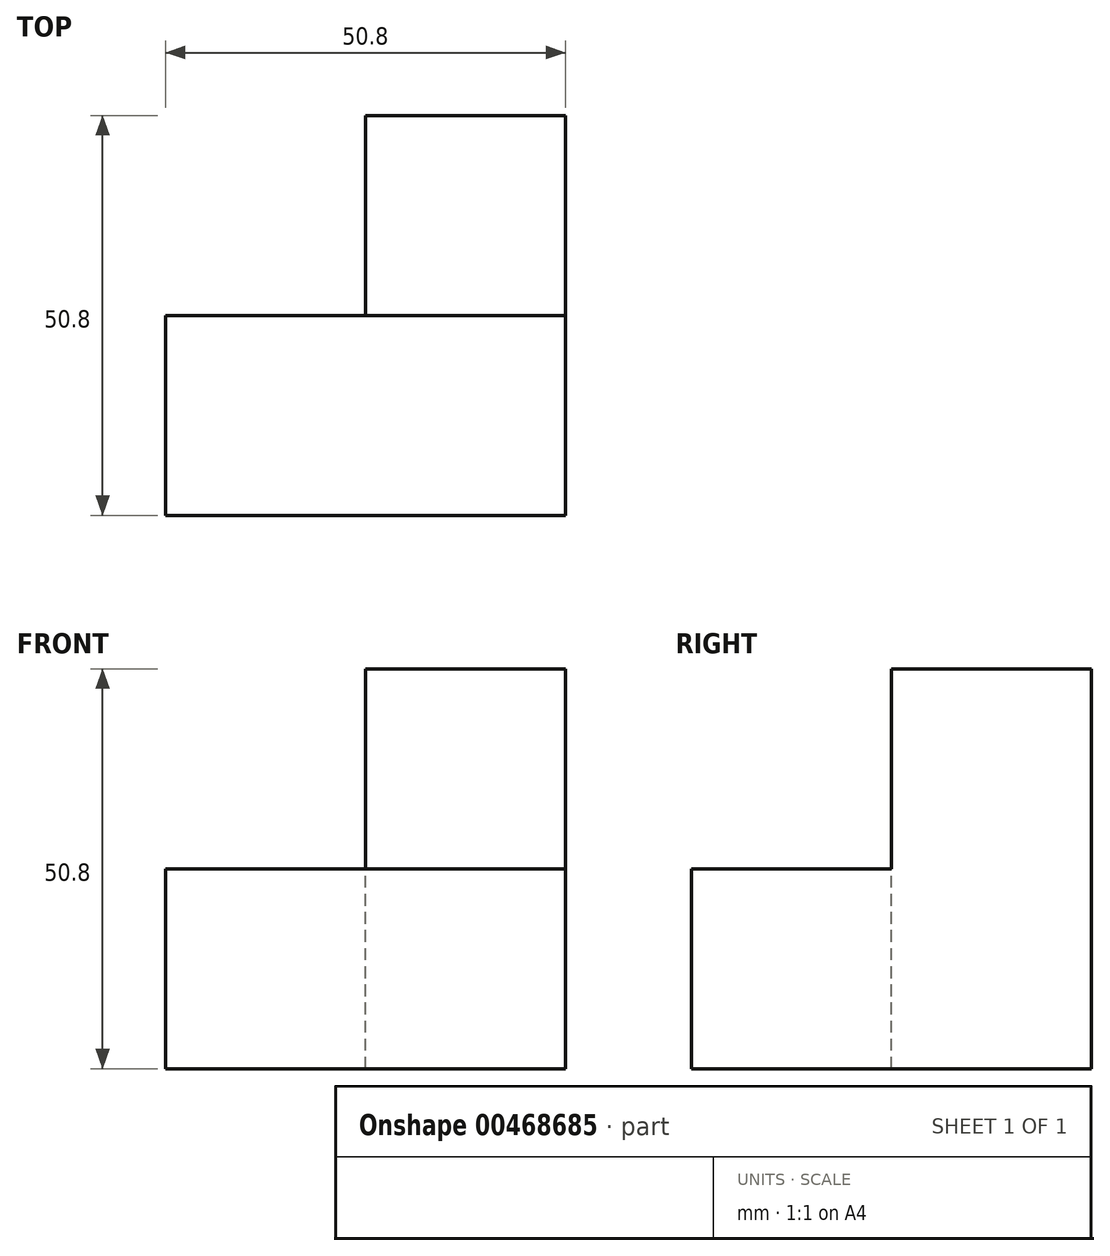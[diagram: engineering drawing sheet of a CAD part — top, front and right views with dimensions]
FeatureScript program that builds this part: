
annotation { "Feature Type Name" : "Feature", "Feature Type Description" : "" }
export const myFeature = defineFeature(function(context is Context, id is Id, definition is map)
    precondition{}
    {
        {
            var Q0;
            Q0=qCreatedBy(makeId("Front.planeOp"),FACE);
            var sketch = newSketch(context, id + "F0", { "sketchPlane" : qUnion([Q0])});
            skLineSegment(sketch, "E0.bottom", {"start": v(-25.4, 0) * mm, "end": v(25.4, 0) * mm});
            skLineSegment(sketch, "E0.top", {"start": v(-25.4, 25.4) * mm, "end": v(25.4, 25.4) * mm});
            skLineSegment(sketch, "E0.left", {"start": v(-25.4, 0) * mm, "end": v(-25.4, 25.4) * mm});
            skLineSegment(sketch, "E0.right", {"start": v(25.4, 0) * mm, "end": v(25.4, 25.4) * mm});
            skSolve(sketch);
        }
        {
            var Q0;
            Q0=qCreatedBy(makeId("Right.planeOp"),FACE);
            var sketch = newSketch(context, id + "F1", { "sketchPlane" : qUnion([Q0])});
            skLineSegment(sketch, "E1.bottom", {"start": v(0, 0) * mm, "end": v(25.4, 0) * mm});
            skLineSegment(sketch, "E1.top", {"start": v(0, 50.8) * mm, "end": v(25.4, 50.8) * mm});
            skLineSegment(sketch, "E1.left", {"start": v(0, 0) * mm, "end": v(0, 50.8) * mm});
            skLineSegment(sketch, "E1.right", {"start": v(25.4, 0) * mm, "end": v(25.4, 50.8) * mm});
            skSolve(sketch);
        }
        {
            var Q0;
            Q0=makeQuery(id+"F1.imprint","IMPRINT",FACE,{"disambiguationData":[TD([[makeQuery(id+"F1.imprint","IMPRINT",EDGE,{"derivedFrom":sQuery(id+"F1.wireOp",EDGE,"E1.bottom")}),1.0]])]});
            extrude(context, id + "F2", {"entities" : qUnion([Q0]), "depth" : 25.4 * mm});
        }
        {
            var Q0;
            Q0=makeQuery(id+"F0.imprint","IMPRINT",FACE,{"disambiguationData":[TD([[makeQuery(id+"F0.imprint","IMPRINT",EDGE,{"derivedFrom":sQuery(id+"F0.wireOp",EDGE,"E0.bottom")}),1.0]])]});
            extrude(context, id + "F3", {"entities" : qUnion([Q0]), "operationType" : NewBodyOperationType.ADD, "depth" : 25.4 * mm});
        }
    });
